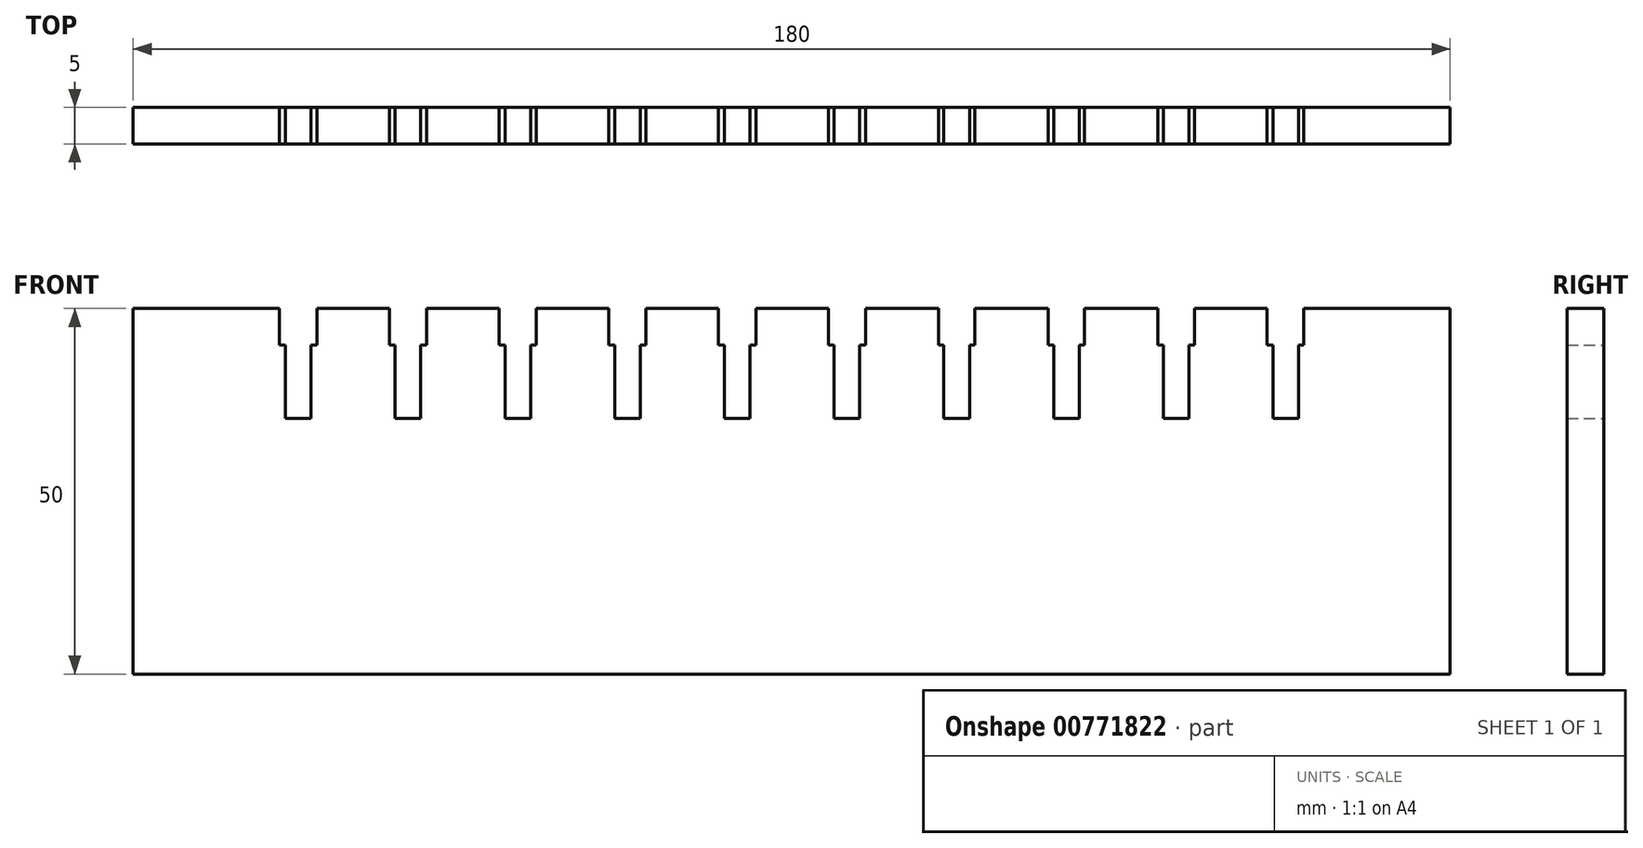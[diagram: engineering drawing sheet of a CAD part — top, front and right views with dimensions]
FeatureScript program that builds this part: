
annotation { "Feature Type Name" : "Feature", "Feature Type Description" : "" }
export const myFeature = defineFeature(function(context is Context, id is Id, definition is map)
    precondition{}
    {
        {
            var Q0;
            Q0=qCreatedBy(makeId("Front.planeOp"),FACE);
            var sketch = newSketch(context, id + "F0", { "sketchPlane" : qUnion([Q0])});
            skLineSegment(sketch, "E0.bottom", {"start": v(-97.55, 25) * mm, "end": v(82.45, 25) * mm});
            skLineSegment(sketch, "E0.top", {"start": v(-97.55, -25) * mm, "end": v(82.45, -25) * mm});
            skLineSegment(sketch, "E0.left", {"start": v(-97.55, 25) * mm, "end": v(-97.55, -25) * mm});
            skLineSegment(sketch, "E0.right", {"start": v(82.45, 25) * mm, "end": v(82.45, -25) * mm});
            skLineSegment(sketch, "E1.bottom", {"start": v(-2.55, 25) * mm, "end": v(2.55, 25) * mm});
            skLineSegment(sketch, "E1.top", {"start": v(-2.55, 20) * mm, "end": v(2.55, 20) * mm});
            skLineSegment(sketch, "E1.left", {"start": v(-2.55, 25) * mm, "end": v(-2.55, 20) * mm});
            skLineSegment(sketch, "E1.right", {"start": v(2.55, 25) * mm, "end": v(2.55, 20) * mm});
            skLineSegment(sketch, "E2.bottom", {"start": v(-1.75, 20) * mm, "end": v(1.75, 20) * mm});
            skLineSegment(sketch, "E2.top", {"start": v(-1.75, 10) * mm, "end": v(1.75, 10) * mm});
            skLineSegment(sketch, "E2.left", {"start": v(-1.75, 20) * mm, "end": v(-1.75, 10) * mm});
            skLineSegment(sketch, "E2.right", {"start": v(1.75, 20) * mm, "end": v(1.75, 10) * mm});
            skLineSegment(sketch, "E3.1.0.0", {"start": v(12.5, 25) * mm, "end": v(17.5, 25) * mm});
            skLineSegment(sketch, "E3.1.0.1", {"start": v(12.5, 25) * mm, "end": v(12.5, 20) * mm});
            skLineSegment(sketch, "E3.1.0.2", {"start": v(17.5, 25) * mm, "end": v(17.5, 20) * mm});
            skLineSegment(sketch, "E3.1.0.3", {"start": v(12.5, 20) * mm, "end": v(17.5, 20) * mm});
            skLineSegment(sketch, "E3.1.0.4", {"start": v(16.75, 20) * mm, "end": v(16.75, 10) * mm});
            skLineSegment(sketch, "E3.1.0.5", {"start": v(13.25, 10) * mm, "end": v(16.75, 10) * mm});
            skLineSegment(sketch, "E3.1.0.6", {"start": v(13.25, 20) * mm, "end": v(13.25, 10) * mm});
            skLineSegment(sketch, "E3.2.0.0", {"start": v(27.5, 25) * mm, "end": v(32.5, 25) * mm});
            skLineSegment(sketch, "E3.2.0.1", {"start": v(27.5, 25) * mm, "end": v(27.5, 20) * mm});
            skLineSegment(sketch, "E3.2.0.2", {"start": v(32.5, 25) * mm, "end": v(32.5, 20) * mm});
            skLineSegment(sketch, "E3.2.0.3", {"start": v(27.5, 20) * mm, "end": v(32.5, 20) * mm});
            skLineSegment(sketch, "E3.2.0.4", {"start": v(31.75, 20) * mm, "end": v(31.75, 10) * mm});
            skLineSegment(sketch, "E3.2.0.5", {"start": v(28.25, 10) * mm, "end": v(31.75, 10) * mm});
            skLineSegment(sketch, "E3.2.0.6", {"start": v(28.25, 20) * mm, "end": v(28.25, 10) * mm});
            skLineSegment(sketch, "E3.3.0.0", {"start": v(42.5, 25) * mm, "end": v(47.5, 25) * mm});
            skLineSegment(sketch, "E3.3.0.1", {"start": v(42.5, 25) * mm, "end": v(42.5, 20) * mm});
            skLineSegment(sketch, "E3.3.0.2", {"start": v(47.5, 25) * mm, "end": v(47.5, 20) * mm});
            skLineSegment(sketch, "E3.3.0.3", {"start": v(42.5, 20) * mm, "end": v(47.5, 20) * mm});
            skLineSegment(sketch, "E3.3.0.4", {"start": v(46.75, 20) * mm, "end": v(46.75, 10) * mm});
            skLineSegment(sketch, "E3.3.0.5", {"start": v(43.25, 10) * mm, "end": v(46.75, 10) * mm});
            skLineSegment(sketch, "E3.3.0.6", {"start": v(43.25, 20) * mm, "end": v(43.25, 10) * mm});
            skLineSegment(sketch, "E3.4.0.0", {"start": v(57.45, 25) * mm, "end": v(62.45, 25) * mm});
            skLineSegment(sketch, "E3.4.0.1", {"start": v(57.45, 25) * mm, "end": v(57.45, 20) * mm});
            skLineSegment(sketch, "E3.4.0.2", {"start": v(62.45, 25) * mm, "end": v(62.45, 20) * mm});
            skLineSegment(sketch, "E3.4.0.3", {"start": v(57.45, 20) * mm, "end": v(62.45, 20) * mm});
            skLineSegment(sketch, "E3.4.0.4", {"start": v(61.75, 20) * mm, "end": v(61.75, 10) * mm});
            skLineSegment(sketch, "E3.4.0.5", {"start": v(58.25, 10) * mm, "end": v(61.75, 10) * mm});
            skLineSegment(sketch, "E3.4.0.6", {"start": v(58.25, 20) * mm, "end": v(58.25, 10) * mm});
            skLineSegment(sketch, "E4.1.0.0", {"start": v(-17.55, 25) * mm, "end": v(-12.45, 25) * mm});
            skLineSegment(sketch, "E4.1.0.1", {"start": v(-12.45, 25) * mm, "end": v(-12.45, 20) * mm});
            skLineSegment(sketch, "E4.1.0.2", {"start": v(-17.55, 25) * mm, "end": v(-17.55, 20) * mm});
            skLineSegment(sketch, "E4.1.0.3", {"start": v(-17.55, 20) * mm, "end": v(-12.45, 20) * mm});
            skLineSegment(sketch, "E4.1.0.4", {"start": v(-16.75, 20) * mm, "end": v(-16.75, 10) * mm});
            skLineSegment(sketch, "E4.1.0.5", {"start": v(-13.25, 20) * mm, "end": v(-13.25, 10) * mm});
            skLineSegment(sketch, "E4.1.0.6", {"start": v(-16.75, 10) * mm, "end": v(-13.25, 10) * mm});
            skLineSegment(sketch, "E4.2.0.0", {"start": v(-32.55, 25) * mm, "end": v(-27.45, 25) * mm});
            skLineSegment(sketch, "E4.2.0.1", {"start": v(-27.45, 25) * mm, "end": v(-27.45, 20) * mm});
            skLineSegment(sketch, "E4.2.0.2", {"start": v(-32.55, 25) * mm, "end": v(-32.55, 20) * mm});
            skLineSegment(sketch, "E4.2.0.3", {"start": v(-32.55, 20) * mm, "end": v(-27.45, 20) * mm});
            skLineSegment(sketch, "E4.2.0.4", {"start": v(-31.75, 20) * mm, "end": v(-31.75, 10) * mm});
            skLineSegment(sketch, "E4.2.0.5", {"start": v(-28.25, 20) * mm, "end": v(-28.25, 10) * mm});
            skLineSegment(sketch, "E4.2.0.6", {"start": v(-31.75, 10) * mm, "end": v(-28.25, 10) * mm});
            skLineSegment(sketch, "E4.3.0.0", {"start": v(-47.55, 25) * mm, "end": v(-42.45, 25) * mm});
            skLineSegment(sketch, "E4.3.0.1", {"start": v(-42.45, 25) * mm, "end": v(-42.45, 20) * mm});
            skLineSegment(sketch, "E4.3.0.2", {"start": v(-47.55, 25) * mm, "end": v(-47.55, 20) * mm});
            skLineSegment(sketch, "E4.3.0.3", {"start": v(-47.55, 20) * mm, "end": v(-42.45, 20) * mm});
            skLineSegment(sketch, "E4.3.0.4", {"start": v(-46.75, 20) * mm, "end": v(-46.75, 10) * mm});
            skLineSegment(sketch, "E4.3.0.5", {"start": v(-43.25, 20) * mm, "end": v(-43.25, 10) * mm});
            skLineSegment(sketch, "E4.3.0.6", {"start": v(-46.75, 10) * mm, "end": v(-43.25, 10) * mm});
            skLineSegment(sketch, "E4.4.0.0", {"start": v(-62.55, 25) * mm, "end": v(-57.45, 25) * mm});
            skLineSegment(sketch, "E4.4.0.1", {"start": v(-57.45, 25) * mm, "end": v(-57.45, 20) * mm});
            skLineSegment(sketch, "E4.4.0.2", {"start": v(-62.55, 25) * mm, "end": v(-62.55, 20) * mm});
            skLineSegment(sketch, "E4.4.0.3", {"start": v(-62.55, 20) * mm, "end": v(-57.45, 20) * mm});
            skLineSegment(sketch, "E4.4.0.4", {"start": v(-61.75, 20) * mm, "end": v(-61.75, 10) * mm});
            skLineSegment(sketch, "E4.4.0.5", {"start": v(-58.25, 20) * mm, "end": v(-58.25, 10) * mm});
            skLineSegment(sketch, "E4.4.0.6", {"start": v(-61.75, 10) * mm, "end": v(-58.25, 10) * mm});
            skLineSegment(sketch, "E4.5.0.0", {"start": v(-77.55, 25) * mm, "end": v(-72.45, 25) * mm});
            skLineSegment(sketch, "E4.5.0.1", {"start": v(-72.45, 25) * mm, "end": v(-72.45, 20) * mm});
            skLineSegment(sketch, "E4.5.0.2", {"start": v(-77.55, 25) * mm, "end": v(-77.55, 20) * mm});
            skLineSegment(sketch, "E4.5.0.3", {"start": v(-77.55, 20) * mm, "end": v(-72.45, 20) * mm});
            skLineSegment(sketch, "E4.5.0.4", {"start": v(-76.75, 20) * mm, "end": v(-76.75, 10) * mm});
            skLineSegment(sketch, "E4.5.0.5", {"start": v(-73.25, 20) * mm, "end": v(-73.25, 10) * mm});
            skLineSegment(sketch, "E4.5.0.6", {"start": v(-76.75, 10) * mm, "end": v(-73.25, 10) * mm});
            skLineSegment(sketch, "E4.direction1", {"start": v(-1.75, 10) * mm, "end": v(-16.75, 10) * mm, "construction": true});
            skSolve(sketch);
        }
        {
            var Q0;
            Q0=makeQuery(id+"F0.imprint","IMPRINT",FACE,{"disambiguationData":[TD([[makeQuery(id+"F0.imprint","IMPRINT",EDGE,{"derivedFrom":sQuery(id+"F0.wireOp",EDGE,"E0.top")}),1.0]])]});
            extrude(context, id + "F1", {"entities" : qUnion([Q0]), "depth" : 5 * mm, "offsetDistance" : 25 * mm});
        }
    });
